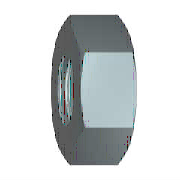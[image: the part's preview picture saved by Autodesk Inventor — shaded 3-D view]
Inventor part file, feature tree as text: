
AUTODESK INVENTOR PART (.ipt)
format: ipt  version: 2020 (Build 240168000, 168)  size: 165,376 bytes
history: native  units: mm (DEFAULTED — no unit token found)
features: sketch x3, extrude x1, chamfer x1, hole x1, other x1, plane x1
ambient origin geometry x7: Origin, YZ Plane, XZ Plane, X Axis, Y Axis, Z Axis, Center Point
bodies: Solid1 (feature_tree)
feature tree (8):
  extrude  "Körper"  Depth=3.2mm
  chamfer  "Fase1"  Angle=30.0deg  [1 undecoded]
  hole  "Gewinde"  [1 undecoded]
  other  "Work Axis1"
  plane  "Work Plane1"
  sketch  "Skizze1"  dims[d0=8.082904mm d1=3.2mm]
  sketch  "Skizze2"  dims[d2=0.0mm]
  sketch  "Skizze3"  dims[d3=30.0deg d4=30.0deg d5=5.9mm d6=5.9mm d7=90.0deg d25=3.242mm d26=6.0mm d27=4.0mm d28=2.0mm d29=14.3117mm d30=8.0mm d31=20.594885mm d8=0.378886mm d9=30.0deg d10=0.378886mm d11=30.0deg d13=0.0mm d14=0.0mm d39=0.0mm d40=0.378886mm d41=0.378886mm d42=0.0mm]
note: 2 required parameter values undecoded (feature->parameter linkage not recoverable at this tier; creation-order binding heuristic only, values carry confidence <= 0.55)
